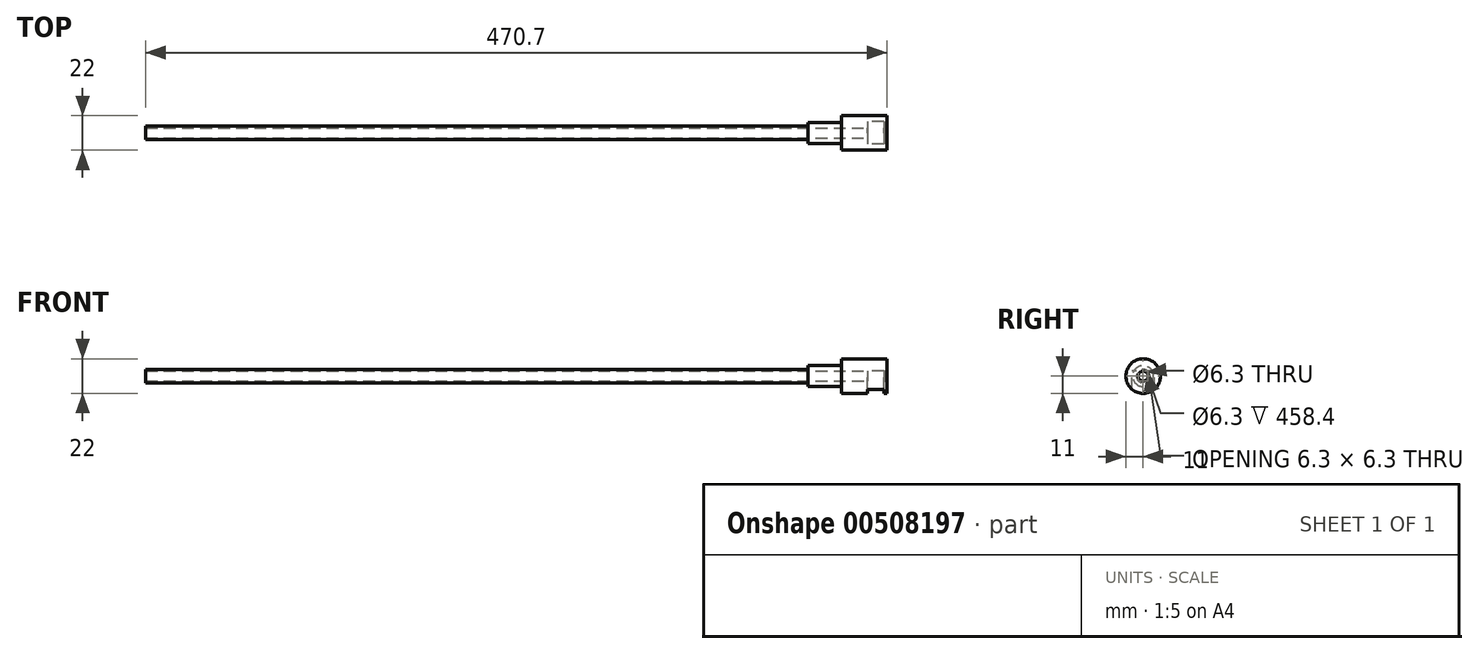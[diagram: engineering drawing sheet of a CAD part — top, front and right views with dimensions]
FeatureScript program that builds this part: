
annotation { "Feature Type Name" : "Feature", "Feature Type Description" : "" }
export const myFeature = defineFeature(function(context is Context, id is Id, definition is map)
    precondition{}
    {
        {
            var Q0;
            Q0=qCreatedBy(makeId("Right.planeOp"),FACE);
            var sketch = newSketch(context, id + "F0", { "sketchPlane" : qUnion([Q0])});
            skCircle(sketch, "E0", {"center": v(0, 0) * mm, "radius": 11 * mm});
            skCircle(sketch, "E1", {"center": v(0, 0) * mm, "radius": 6.65 * mm});
            skCircle(sketch, "E2", {"center": v(0, 0) * mm, "radius": 4.25 * mm});
            skCircle(sketch, "E3", {"center": v(0, 0) * mm, "radius": 3.15 * mm});
            skSolve(sketch);
        }
        {
            var Q0;
            Q0=makeQuery(id+"F0.imprint","IMPRINT",FACE,{"disambiguationData":[TD([[makeQuery(id+"F0.imprint","IMPRINT",EDGE,{"derivedFrom":sQuery(id+"F0.wireOp",EDGE,"E2")}),1.0]])]});
            extrude(context, id + "F1", {"entities" : qUnion([Q0]), "oppositeDirection" : true, "depth" : 442 * mm, "offsetDistance" : 25 * mm});
        }
        {
            var Q0;
            Q0=makeQuery(id+"F0.imprint","IMPRINT",FACE,{"disambiguationData":[TD([[makeQuery(id+"F0.imprint","IMPRINT",EDGE,{"derivedFrom":sQuery(id+"F0.wireOp",EDGE,"E1")}),1.0]])]});
            extrude(context, id + "F2", {"entities" : qUnion([Q0]), "operationType" : NewBodyOperationType.ADD, "oppositeDirection" : true, "depth" : 21.5 * mm, "offsetDistance" : 25 * mm});
        }
        {
            var Q0;
            Q0=makeQuery(id+"F0.imprint","IMPRINT",FACE,{"disambiguationData":[TD([[makeQuery(id+"F0.imprint","IMPRINT",EDGE,{"derivedFrom":sQuery(id+"F0.wireOp",EDGE,"E0")}),1.0]])]});
            var Q1;
            Q1=makeQuery(id+"F0.imprint","IMPRINT",FACE,{"disambiguationData":[TD([[makeQuery(id+"F0.imprint","IMPRINT",EDGE,{"derivedFrom":sQuery(id+"F0.wireOp",EDGE,"E1")}),1.0]])]});
            var Q2;
            Q2=makeQuery(id+"F0.imprint","IMPRINT",FACE,{"disambiguationData":[TD([[makeQuery(id+"F0.imprint","IMPRINT",EDGE,{"derivedFrom":sQuery(id+"F0.wireOp",EDGE,"E2")}),1.0]])]});
            extrude(context, id + "F3", {"entities" : qUnion([Q0, Q1, Q2]), "operationType" : NewBodyOperationType.ADD, "depth" : 28.7 * mm, "offsetDistance" : 25 * mm});
        }
        {
            var Q0;
            Q0=qCreatedBy(makeId("Top.planeOp"),FACE);
            var sketch = newSketch(context, id + "F4", { "sketchPlane" : qUnion([Q0])});
            skLineSegment(sketch, "E4.bottom", {"start": v(26.9, 7.15) * mm, "end": v(16.4, 7.15) * mm});
            skLineSegment(sketch, "E4.top", {"start": v(26.9, -7.15) * mm, "end": v(16.4, -7.15) * mm});
            skLineSegment(sketch, "E4.left", {"start": v(26.9, 7.15) * mm, "end": v(26.9, -7.15) * mm});
            skLineSegment(sketch, "E4.right", {"start": v(16.4, 7.15) * mm, "end": v(16.4, -7.15) * mm});
            skPoint(sketch, "E4.middle", {"position": v(21.65, 0) * mm});
            skSolve(sketch);
        }
        {
            var Q0;
            Q0 = qSketchRegion(id + "F4", true);
            extrude(context, id + "F5", {"entities" : qUnion([Q0]), "operationType" : NewBodyOperationType.REMOVE, "endBound" : BoundingType.THROUGH_ALL, "oppositeDirection" : true, "depth" : 25 * mm, "offsetDistance" : 25 * mm, "hasSecondDirection" : true, "secondDirectionOppositeDirection" : false, "secondDirectionDepth" : 3.4 * mm});
        }
    });
